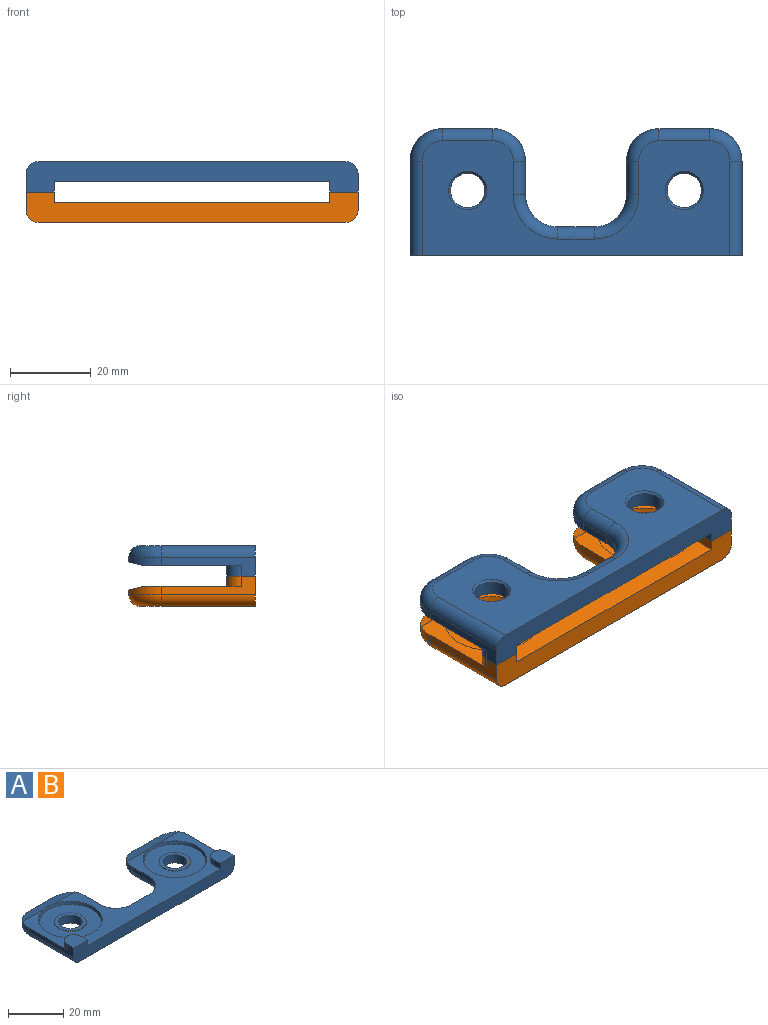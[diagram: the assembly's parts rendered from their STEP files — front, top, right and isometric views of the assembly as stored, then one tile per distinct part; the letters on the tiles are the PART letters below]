
ASSEMBLY  parts=2 mates=1
PART A: 49 faces, bbox 83.3x31.9x7.5 mm
  f0: plane 82x27.25mm, normal (0,0,1), area 833.3mm2, adj f1,f2,f4,f5,f6,f8,f18,f20
  f1: plane 82x7.5mm, normal (0,-1,0), area 441.1mm2, adj f0,f2,f8,f9,f18,f19,f20,f21
  f2: plane 23.25x4.5mm, normal (1,0,0), area 55.3mm2, adj f0,f1,f19,f22,f42,f43
  f3: plane 12.5x1mm, normal (0,1,0), area 12.5mm2, adj f22,f23,f28,f40
  f4: plane 8.25x2mm, normal (-1,0,0), area 16.5mm2, adj f0,f23,f24,f38
  f5: plane 9x2mm, normal (0,1,0), area 18mm2, adj f0,f24,f25,f36
  f6: plane 8.25x2mm, normal (1,0,0), area 16.5mm2, adj f0,f25,f26,f34
  f7: plane 12.5x1mm, normal (0,1,0), area 12.5mm2, adj f26,f27,f29,f32
  f8: plane 23.25x4.5mm, normal (-1,0,0), area 55.3mm2, adj f0,f1,f21,f27,f30,f44
  f9: plane 76x28.25mm, normal (0,0,-1), area 1284mm2, adj f1,f30,f31,f32,f33,f34,f35,f36
  f10: cylinder r=4.25mm len=8.5mm, axis (0,0,-1), area 93.5mm2, adj f15,f47
  f11: plane 22.5x22.5mm, normal (0,0,1), area 293.7mm2, adj f14,f46
  f12: cylinder r=4.25mm len=8.5mm, axis (0,0,-1), area 93.5mm2, adj f17,f48
  f13: plane 22.5x22.5mm, normal (0,0,1), area 293.7mm2, adj f16,f45
  f14: cylinder r=5.75mm len=11.5mm, axis (0,0,-1), area 9mm2, adj f11,f15
  f15: plane 11.5x11.5mm, normal (0,0,1), area 47.1mm2, adj f10,f14
  f16: cylinder r=5.75mm len=11.5mm, axis (0,0,-1), area 9mm2, adj f13,f17
  f17: plane 11.5x11.5mm, normal (0,0,1), area 47.1mm2, adj f12,f16
  f18: plane 3.5x2.5mm, normal (-1,0,0), area 8.7mm2, adj f0,f1,f19,f43
  f19: plane 7x7mm, normal (0,0,1), area 43.7mm2, adj f1,f2,f18,f43
  f20: plane 3.5x2.5mm, normal (1,0,0), area 8.7mm2, adj f0,f1,f21,f44
  f21: plane 7x7mm, normal (0,0,1), area 43.7mm2, adj f1,f8,f20,f44
  f22: cylinder r=8mm len=8mm, axis (0,0,1), area 19.7mm2, adj f0,f2,f3,f28,f41
  f23: cylinder r=8mm len=8mm, axis (0,0,1), area 19.7mm2, adj f0,f3,f4,f28,f39
  f24: cylinder r=8mm len=8mm, axis (0,0,1), area 25.1mm2, adj f0,f4,f5,f37
  f25: cylinder r=8mm len=8mm, axis (0,0,-1), area 25.1mm2, adj f0,f5,f6,f35
  f26: cylinder r=8mm len=8mm, axis (0,0,-1), area 19.7mm2, adj f0,f6,f7,f29,f33
  f27: cylinder r=8mm len=8mm, axis (0,0,-1), area 19.7mm2, adj f0,f7,f8,f29,f31
  f28: plane 26.36x4mm, normal (0,0.24,0.97), area 91.3mm2, adj f0,f3,f22,f23,f45
  f29: plane 26.36x4mm, normal (0,0.24,0.97), area 91.3mm2, adj f0,f7,f26,f27,f46
  f30: cylinder r=3mm len=23.25mm, axis (0,-1,0), area 109.6mm2, adj f1,f8,f9,f31
  f31: torus R=5mm, axis (0,0,1), area 51.1mm2, adj f9,f27,f30,f32
  f32: cylinder r=3mm len=12.5mm, axis (-1,0,0), area 58.9mm2, adj f7,f9,f31,f33
  f33: torus R=5mm, axis (0,0,1), area 51.1mm2, adj f9,f26,f32,f34
  f34: cylinder r=3mm len=8.25mm, axis (0,1,0), area 38.9mm2, adj f6,f9,f33,f35
  f35: torus R=11mm, axis (0,0,1), area 67.3mm2, adj f9,f25,f34,f36
  f36: cylinder r=3mm len=9mm, axis (-1,0,0), area 42.4mm2, adj f5,f9,f35,f37
  f37: torus R=11mm, axis (0,0,1), area 67.3mm2, adj f9,f24,f36,f38
  f38: cylinder r=3mm len=8.25mm, axis (0,-1,0), area 38.9mm2, adj f4,f9,f37,f39
  f39: torus R=5mm, axis (0,0,1), area 51.1mm2, adj f9,f23,f38,f40
  f40: cylinder r=3mm len=12.5mm, axis (-1,0,0), area 58.9mm2, adj f3,f9,f39,f41
  f41: torus R=5mm, axis (0,0,1), area 51.1mm2, adj f9,f22,f40,f42
  f42: cylinder r=3mm len=23.25mm, axis (0,1,0), area 109.6mm2, adj f1,f2,f9,f41
  f43: cylinder r=3.5mm len=7mm, axis (0,0,-1), area 27.5mm2, adj f0,f2,f18,f19
  f44: cylinder r=3.5mm len=7mm, axis (0,0,-1), area 27.5mm2, adj f0,f8,f20,f21
  f45: cone r=11.5mm half-angle=11.3deg, axis (0,0,1), area 90.9mm2, adj f0,f13,f28
  f46: cone r=11.25mm half-angle=11.3deg, axis (0,0,1), area 90.9mm2, adj f0,f11,f29
  f47: cone r=4.25mm half-angle=45deg, axis (0,0,-1), area 20mm2, adj f9,f10
  f48: cone r=4.75mm half-angle=45deg, axis (0,0,-1), area 20mm2, adj f9,f12
PART B: same geometry as A
PLACE A rot(axis=(0,1,0),180deg) t=(-9.48,-10.97,6.75)mm
PLACE B t=(-9.48,-10.97,-8.25)mm
MATE fastened A.f44 <-> B.f43  axis (0,0,-1) through (28.02,-10.97,-0.75)mm
